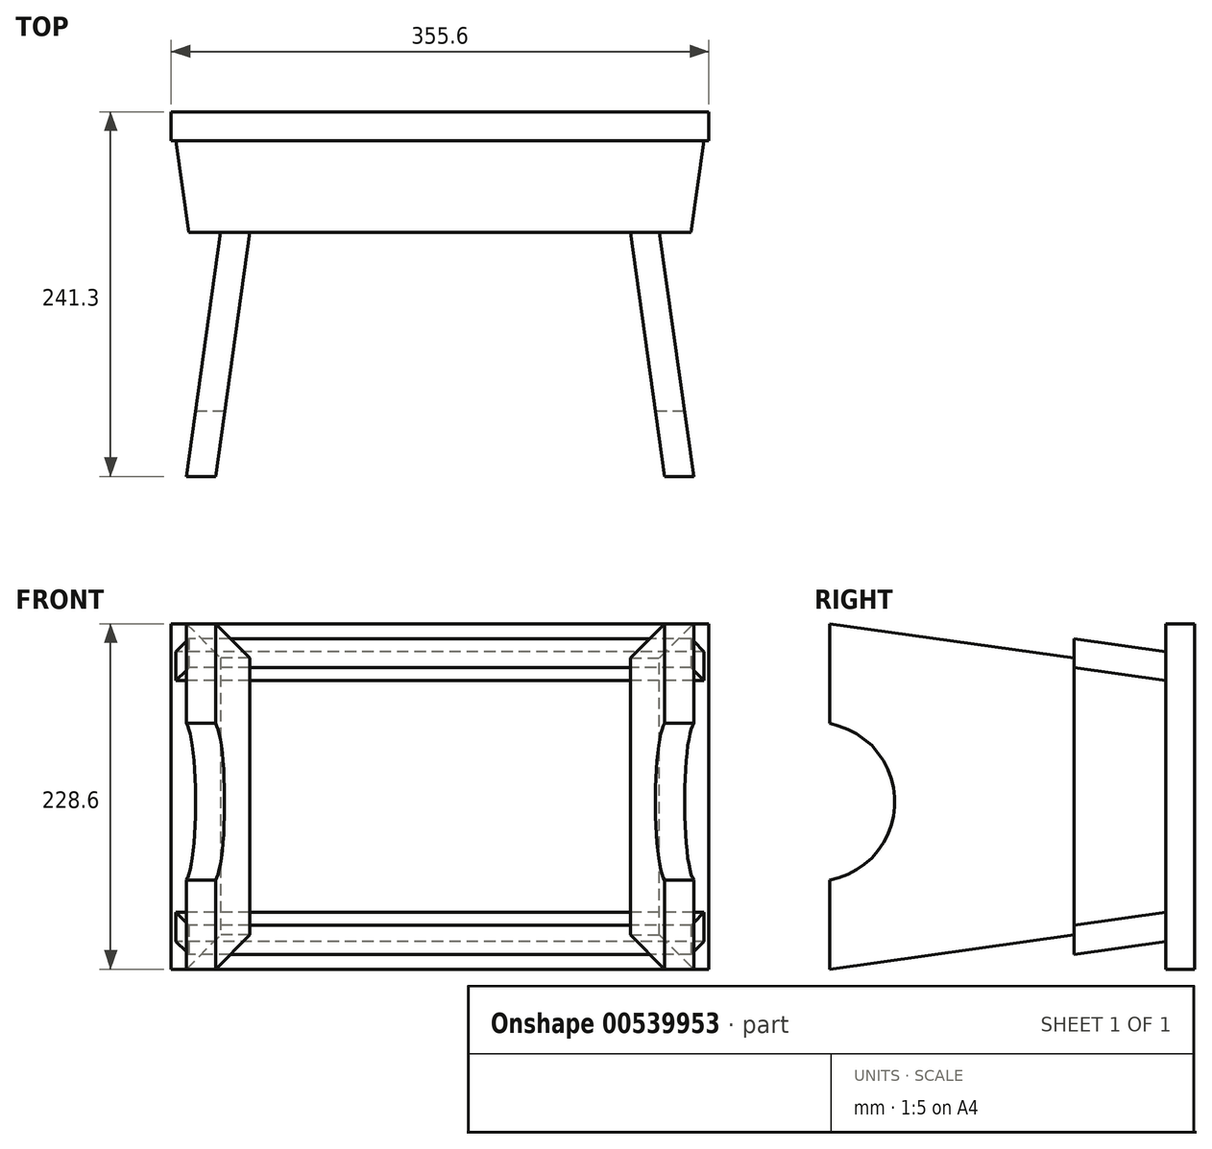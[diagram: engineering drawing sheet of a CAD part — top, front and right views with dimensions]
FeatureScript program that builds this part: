
annotation { "Feature Type Name" : "Feature", "Feature Type Description" : "" }
export const myFeature = defineFeature(function(context is Context, id is Id, definition is map)
    precondition{}
    {
        {
            var Q0;
            Q0=qCreatedBy(makeId("Top.planeOp"),FACE);
            var sketch = newSketch(context, id + "F0", { "sketchPlane" : qUnion([Q0])});
            skLineSegment(sketch, "E0.bottom", {"start": v(-177.8, -19.05) * mm, "end": v(177.8, -19.05) * mm});
            skLineSegment(sketch, "E0.top", {"start": v(-177.8, 0) * mm, "end": v(177.8, 0) * mm});
            skLineSegment(sketch, "E0.left", {"start": v(-177.8, 0) * mm, "end": v(-177.8, -19.05) * mm});
            skLineSegment(sketch, "E0.right", {"start": v(177.8, 0) * mm, "end": v(177.8, -19.05) * mm});
            skLineSegment(sketch, "E1.bottom", {"start": v(-177.8, 0) * mm, "end": v(-179.82, 0) * mm, "construction": true});
            skLineSegment(sketch, "E1.top", {"start": v(-177.8, 0) * mm, "end": v(-179.82, 0) * mm, "construction": true});
            skLineSegment(sketch, "E1.left", {"start": v(-179.82, 0) * mm, "end": v(-179.82, 0) * mm});
            skLineSegment(sketch, "E1.right", {"start": v(-177.8, 0) * mm, "end": v(-177.8, 0) * mm});
            skLineSegment(sketch, "E2.bottom", {"start": v(-177.8, 0) * mm, "end": v(177.8, 0) * mm, "construction": true});
            skLineSegment(sketch, "E2.top", {"start": v(-177.8, -241.3) * mm, "end": v(177.8, -241.3) * mm, "construction": true});
            skLineSegment(sketch, "E2.left", {"start": v(-177.8, 0) * mm, "end": v(-177.8, -241.3) * mm, "construction": true});
            skLineSegment(sketch, "E2.right", {"start": v(177.8, 0) * mm, "end": v(177.8, -241.3) * mm, "construction": true});
            skLineSegment(sketch, "E3", {"start": v(136.51, -19.05) * mm, "end": v(167.75, -241.3) * mm});
            skLineSegment(sketch, "E4", {"start": v(148.51, -241.3) * mm, "end": v(117.28, -19.05) * mm});
            skLineSegment(sketch, "E5", {"start": v(167.75, -241.3) * mm, "end": v(148.51, -241.3) * mm});
            skLineSegment(sketch, "E6", {"start": v(117.28, -19.05) * mm, "end": v(136.51, -19.05) * mm});
            skLineSegment(sketch, "E7", {"start": v(0, 0) * mm, "end": v(0, -241.3) * mm});
            skLineSegment(sketch, "E8", {"start": v(0, -241.3) * mm, "end": v(0, -244.61) * mm});
            skPoint(sketch, "E8.endSnap0", {"position": v(0, -120.65) * mm});
            skLineSegment(sketch, "E9.MirrorCS", {"start": v(-117.28, -19.05) * mm, "end": v(-136.51, -19.05) * mm});
            skLineSegment(sketch, "E10.MirrorCS", {"start": v(-167.75, -241.3) * mm, "end": v(-148.51, -241.3) * mm});
            skLineSegment(sketch, "E11.MirrorCS", {"start": v(-148.51, -241.3) * mm, "end": v(-117.28, -19.05) * mm});
            skLineSegment(sketch, "E12.MirrorCS", {"start": v(-136.51, -19.05) * mm, "end": v(-167.75, -241.3) * mm});
            skLineSegment(sketch, "E13", {"start": v(174.62, -19.05) * mm, "end": v(166.07, -79.9) * mm});
            skLineSegment(sketch, "E14.MirrorCS", {"start": v(-174.62, -19.05) * mm, "end": v(-166.07, -79.9) * mm});
            skLineSegment(sketch, "E15", {"start": v(-177.8, -79.9) * mm, "end": v(177.8, -79.9) * mm});
            skLineSegment(sketch, "E16", {"start": v(177.8, -79.9) * mm, "end": v(177.8, -19.05) * mm});
            skLineSegment(sketch, "E17", {"start": v(-177.8, -79.9) * mm, "end": v(-177.8, -19.05) * mm});
            skSolve(sketch);
        }
        {
            var Q0;
            Q0=makeQuery(id+"F0.imprint","IMPRINT",FACE,{"disambiguationData":[TD([[makeQuery(id+"F0.imprint","IMPRINT",EDGE,{"derivedFrom":sQuery(id+"F0.wireOp",EDGE,"E0.top")}),-1.0]])]});
            extrude(context, id + "F1", {"entities" : qUnion([Q0]), "depth" : 228.6 * mm, "offsetDistance" : 25.4 * mm, "symmetric" : true});
        }
        {
            var Q0;
            {var subQ0=sQuery(id+"F0.wireOp",EDGE,"E6");Q0=makeQuery(id+"F0.imprint","IMPRINT",FACE,{"disambiguationData":[TD([[makeQuery(id+"F0.imprint","IMPRINT",EDGE,{"derivedFrom":subQ0}),-1.0]])]});}
            var Q1;
            {var subQ0=sQuery(id+"F0.wireOp",EDGE,"E5");Q1=makeQuery(id+"F0.imprint","IMPRINT",FACE,{"disambiguationData":[TD([[makeQuery(id+"F0.imprint","IMPRINT",EDGE,{"derivedFrom":subQ0}),-1.0]])]});}
            var Q2;
            Q2=makeQuery(id+"F1.opExtrude","CAP_VERTEX",VERTEX,{"disambiguationData":[OSD([sQuery(id+"F0.wireOp",EDGE,"E0.top"),sQuery(id+"F0.wireOp",EDGE,"E0.right")])],"isStart":true});
            var Q3;
            Q3=makeQuery(id+"F1.opExtrude","CAP_VERTEX",VERTEX,{"disambiguationData":[OSD([sQuery(id+"F0.wireOp",EDGE,"E0.top"),sQuery(id+"F0.wireOp",EDGE,"E0.right")])],"isStart":false});
            extrude(context, id + "F2", {"entities" : qUnion([Q0, Q1]), "endBound" : BoundingType.UP_TO_VERTEX, "oppositeDirection" : true, "depth" : 25.4 * mm, "endBoundEntityVertex" : qUnion([Q2]), "offsetDistance" : 25.4 * mm, "hasSecondDirection" : true, "secondDirectionBound" : BoundingType.UP_TO_VERTEX, "secondDirectionOppositeDirection" : false, "secondDirectionDepth" : 25.4 * mm, "secondDirectionBoundEntityVertex" : qUnion([Q3])});
        }
        {
            var Q0;
            {var subQ0=sQuery(id+"F0.wireOp",EDGE,"E9.MirrorCS");Q0=makeQuery(id+"F0.imprint","IMPRINT",FACE,{"disambiguationData":[TD([[makeQuery(id+"F0.imprint","IMPRINT",EDGE,{"derivedFrom":subQ0}),1.0]])]});}
            var Q1;
            {var subQ0=sQuery(id+"F0.wireOp",EDGE,"E10.MirrorCS");Q1=makeQuery(id+"F0.imprint","IMPRINT",FACE,{"disambiguationData":[TD([[makeQuery(id+"F0.imprint","IMPRINT",EDGE,{"derivedFrom":subQ0}),1.0]])]});}
            var Q2;
            Q2=makeQuery(id+"F1.opExtrude","CAP_VERTEX",VERTEX,{"disambiguationData":[OSD([sQuery(id+"F0.wireOp",EDGE,"E0.top"),sQuery(id+"F0.wireOp",EDGE,"E0.left")])],"isStart":false});
            var Q3;
            Q3=makeQuery(id+"F1.opExtrude","CAP_VERTEX",VERTEX,{"disambiguationData":[OSD([sQuery(id+"F0.wireOp",EDGE,"E0.top"),sQuery(id+"F0.wireOp",EDGE,"E0.left")])],"isStart":true});
            extrude(context, id + "F3", {"entities" : qUnion([Q0, Q1]), "endBound" : BoundingType.UP_TO_VERTEX, "depth" : 25.4 * mm, "endBoundEntityVertex" : qUnion([Q2]), "offsetDistance" : 25.4 * mm, "hasSecondDirection" : true, "secondDirectionBound" : BoundingType.UP_TO_VERTEX, "secondDirectionOppositeDirection" : true, "secondDirectionDepth" : 25.4 * mm, "secondDirectionBoundEntityVertex" : qUnion([Q3])});
        }
        {
            var Q0;
            Q0=qCreatedBy(makeId("Right.planeOp"),FACE);
            var sketch = newSketch(context, id + "F4", { "sketchPlane" : qUnion([Q0])});
            skLineSegment(sketch, "E18.0.0", {"start": v(-19.05, -114.3) * mm, "end": v(-19.05, 114.3) * mm});
            skLineSegment(sketch, "E18.0.1", {"start": v(-19.05, 114.3) * mm, "end": v(-241.3, 114.3) * mm});
            skLineSegment(sketch, "E18.0.2", {"start": v(-241.3, 114.3) * mm, "end": v(-241.3, -114.3) * mm});
            skLineSegment(sketch, "E18.0.3", {"start": v(-241.3, -114.3) * mm, "end": v(-19.05, -114.3) * mm});
            skLineSegment(sketch, "E19", {"start": v(-241.3, 114.3) * mm, "end": v(-19.05, 83.06) * mm});
            skLineSegment(sketch, "E20.MirrorCS", {"start": v(-241.3, -114.3) * mm, "end": v(-19.05, -83.06) * mm});
            skArc(sketch, "E21", {"start": v(-241.3, -55.42) * mm, "mid": v(-198.1, -3.53) * mm, "end": v(-241.3, 48.35) * mm});
            skLineSegment(sketch, "E22", {"start": v(-250.87, -3.53) * mm, "end": v(-241.3, 0) * mm, "construction": true});
            skSolve(sketch);
        }
        {
            var Q0;
            {var subQ0=sQuery(id+"F4.wireOp",EDGE,"E21");Q0=makeQuery(id+"F4.imprint","IMPRINT",FACE,{"disambiguationData":[TD([[makeQuery(id+"F4.imprint","IMPRINT",EDGE,{"derivedFrom":subQ0}),1.0]])]});}
            var Q1;
            {var subQ0=sQuery(id+"F4.wireOp",EDGE,"E18.0.3");Q1=makeQuery(id+"F4.imprint","IMPRINT",FACE,{"disambiguationData":[TD([[makeQuery(id+"F4.imprint","IMPRINT",EDGE,{"derivedFrom":subQ0}),1.0]])]});}
            var Q2;
            {var subQ0=sQuery(id+"F4.wireOp",EDGE,"E18.0.1");Q2=makeQuery(id+"F4.imprint","IMPRINT",FACE,{"disambiguationData":[TD([[makeQuery(id+"F4.imprint","IMPRINT",EDGE,{"derivedFrom":subQ0}),1.0]])]});}
            extrude(context, id + "F5", {"entities" : qUnion([Q0, Q1, Q2]), "operationType" : NewBodyOperationType.REMOVE, "endBound" : BoundingType.THROUGH_ALL, "oppositeDirection" : true, "depth" : 25.4 * mm, "offsetDistance" : 25.4 * mm, "hasSecondDirection" : true, "secondDirectionBound" : BoundingType.THROUGH_ALL, "secondDirectionOppositeDirection" : false, "secondDirectionDepth" : 25.4 * mm});
        }
        {
            var Q0;
            Q0=qCreatedBy(makeId("Right.planeOp"),FACE);
            var sketch = newSketch(context, id + "F6", { "sketchPlane" : qUnion([Q0])});
            skLineSegment(sketch, "E23.0", {"start": v(-19.05, 83.06) * mm, "end": v(-241.3, 114.3) * mm});
            skLineSegment(sketch, "E24.0", {"start": v(-19.05, 114.3) * mm, "end": v(-19.05, -114.3) * mm});
            skLineSegment(sketch, "E25.0", {"start": v(-19.05, -83.06) * mm, "end": v(-241.3, -114.3) * mm});
            skLineSegment(sketch, "E26", {"start": v(-19.05, 95.89) * mm, "end": v(-79.9, 104.44) * mm});
            skLineSegment(sketch, "E27", {"start": v(-79.9, 104.44) * mm, "end": v(-79.9, 85.2) * mm});
            skLineSegment(sketch, "E28", {"start": v(-79.9, 85.2) * mm, "end": v(-19.05, 76.65) * mm});
            skLineSegment(sketch, "E29", {"start": v(-79.9, 85.2) * mm, "end": v(-79.9, -22.26) * mm, "construction": true});
            skLineSegment(sketch, "E30.MirrorCS", {"start": v(-79.9, -85.2) * mm, "end": v(-79.9, 22.26) * mm, "construction": true});
            skLineSegment(sketch, "E31.MirrorCS", {"start": v(-79.9, -85.2) * mm, "end": v(-19.05, -76.65) * mm});
            skLineSegment(sketch, "E32.MirrorCS", {"start": v(-19.05, -95.89) * mm, "end": v(-79.9, -104.44) * mm});
            skLineSegment(sketch, "E33.MirrorCS", {"start": v(-79.9, -104.44) * mm, "end": v(-79.9, -85.2) * mm});
            skSolve(sketch);
        }
        {
            var Q0;
            {var subQ3=sQuery(id+"F6.wireOp",EDGE,"E31.MirrorCS");Q0=makeQuery(id+"F6.imprint","IMPRINT",FACE,{"disambiguationData":[TD([[makeQuery(id+"F6.imprint","IMPRINT",EDGE,{"derivedFrom":subQ3}),-1.0]])]});}
            var Q1;
            {var subQ3=sQuery(id+"F6.wireOp",EDGE,"E32.MirrorCS");Q1=makeQuery(id+"F6.imprint","IMPRINT",FACE,{"disambiguationData":[TD([[makeQuery(id+"F6.imprint","IMPRINT",EDGE,{"derivedFrom":subQ3}),-1.0]])]});}
            var Q2;
            {var subQ5=sQuery(id+"F6.wireOp",EDGE,"E28");Q2=makeQuery(id+"F6.imprint","IMPRINT",FACE,{"disambiguationData":[TD([[makeQuery(id+"F6.imprint","IMPRINT",EDGE,{"derivedFrom":subQ5}),1.0]])]});}
            var Q3;
            {var subQ5=sQuery(id+"F6.wireOp",EDGE,"E26");Q3=makeQuery(id+"F6.imprint","IMPRINT",FACE,{"disambiguationData":[TD([[makeQuery(id+"F6.imprint","IMPRINT",EDGE,{"derivedFrom":subQ5}),1.0]])]});}
            var Q4;
            Q4=makeQuery(id+"F1.opExtrude","SWEPT_FACE",FACE,{"disambiguationData":[OSD([sQuery(id+"F0.wireOp",EDGE,"E0.left")])]});
            var Q5;
            Q5=makeQuery(id+"F1.opExtrude","CAP_VERTEX",VERTEX,{"disambiguationData":[OSD([sQuery(id+"F0.wireOp",EDGE,"E0.bottom"),sQuery(id+"F0.wireOp",EDGE,"E0.right")])],"isStart":true});
            var Q6;
            Q6=makeQuery(id+"F1.opExtrude","CAP_VERTEX",VERTEX,{"disambiguationData":[OSD([sQuery(id+"F0.wireOp",EDGE,"E0.bottom"),sQuery(id+"F0.wireOp",EDGE,"E0.left")])],"isStart":true});
            extrude(context, id + "F7", {"entities" : qUnion([Q0, Q1, Q2, Q3]), "endBound" : BoundingType.UP_TO_VERTEX, "depth" : 159 * mm, "endBoundEntityFace" : qUnion([Q4]), "endBoundEntityVertex" : qUnion([Q5]), "offsetDistance" : 25.4 * mm, "hasSecondDirection" : true, "secondDirectionBound" : BoundingType.UP_TO_VERTEX, "secondDirectionOppositeDirection" : true, "secondDirectionDepth" : 25.4 * mm, "secondDirectionBoundEntityVertex" : qUnion([Q6])});
        }
        {
            var Q0;
            {var subQ2=sQuery(id+"F0.wireOp",EDGE,"E13");Q0=makeQuery(id+"F0.imprint","IMPRINT",FACE,{"disambiguationData":[TD([[makeQuery(id+"F0.imprint","IMPRINT",EDGE,{"derivedFrom":subQ2}),1.0]])]});}
            var Q1;
            {var subQ2=sQuery(id+"F0.wireOp",EDGE,"E14.MirrorCS");Q1=makeQuery(id+"F0.imprint","IMPRINT",FACE,{"disambiguationData":[TD([[makeQuery(id+"F0.imprint","IMPRINT",EDGE,{"derivedFrom":subQ2}),-1.0]])]});}
            var Q2;
            Q2=sQuery(id+"F0.wireOp",EDGE,"E13");
            var Q3;
            Q3=sQuery(id+"F0.wireOp",EDGE,"E16");
            var Q4;
            Q4=makeQuery(id+"F1.opExtrude","CAP_FACE",FACE,{"disambiguationData":[OSD([sQuery(id+"F0.wireOp",EDGE,"E0.bottom"),sQuery(id+"F0.wireOp",EDGE,"E0.top"),sQuery(id+"F0.wireOp",EDGE,"E0.left"),sQuery(id+"F0.wireOp",EDGE,"E0.right"),sQuery(id+"F0.wireOp",EDGE,"E6"),sQuery(id+"F0.wireOp",EDGE,"E9.MirrorCS")])],"isStart":false});
            var Q5;
            Q5=makeQuery(id+"F1.opExtrude","CAP_FACE",FACE,{"disambiguationData":[OSD([sQuery(id+"F0.wireOp",EDGE,"E0.bottom"),sQuery(id+"F0.wireOp",EDGE,"E0.top"),sQuery(id+"F0.wireOp",EDGE,"E0.left"),sQuery(id+"F0.wireOp",EDGE,"E0.right"),sQuery(id+"F0.wireOp",EDGE,"E6"),sQuery(id+"F0.wireOp",EDGE,"E9.MirrorCS")])],"isStart":true});
            extrude(context, id + "F8", {"entities" : qUnion([Q0, Q1]), "operationType" : NewBodyOperationType.REMOVE, "surfaceEntities" : qUnion([Q2, Q3]), "endBound" : BoundingType.UP_TO_SURFACE, "depth" : 25.4 * mm, "endBoundEntityFace" : qUnion([Q4]), "offsetDistance" : 25.4 * mm, "hasSecondDirection" : true, "secondDirectionBound" : BoundingType.UP_TO_SURFACE, "secondDirectionOppositeDirection" : true, "secondDirectionDepth" : 25.4 * mm, "secondDirectionBoundEntityFace" : qUnion([Q5])});
        }
        {
            var Q0;
            Q0=makeQuery(id+"F3.opExtrude","SWEPT_BODY",BODY,{"disambiguationData":[OSD([sQuery(id+"F0.wireOp",EDGE,"E9.MirrorCS"),sQuery(id+"F0.wireOp",EDGE,"E10.MirrorCS"),sQuery(id+"F0.wireOp",EDGE,"E11.MirrorCS"),sQuery(id+"F0.wireOp",EDGE,"E12.MirrorCS")])]});
            var Q1;
            Q1=makeQuery(id+"F7.opExtrude","SWEPT_BODY",BODY,{"disambiguationData":[OSD([sQuery(id+"F6.wireOp",EDGE,"E24.0"),sQuery(id+"F6.wireOp",EDGE,"E26"),sQuery(id+"F6.wireOp",EDGE,"E27"),sQuery(id+"F6.wireOp",EDGE,"E28")])]});
            booleanBodies(context, id + "F9", {"operationType" : BooleanOperationType.SUBTRACTION, "tools" : qUnion([Q0]), "targets" : qUnion([Q1]), "keepTools" : true});
        }
        {
            var Q0;
            Q0=makeQuery(id+"F2.opExtrude","SWEPT_BODY",BODY,{"disambiguationData":[OSD([sQuery(id+"F0.wireOp",EDGE,"E3"),sQuery(id+"F0.wireOp",EDGE,"E4"),sQuery(id+"F0.wireOp",EDGE,"E5"),sQuery(id+"F0.wireOp",EDGE,"E6")])]});
            var Q1;
            Q1=makeQuery(id+"F7.opExtrude","SWEPT_BODY",BODY,{"disambiguationData":[OSD([sQuery(id+"F6.wireOp",EDGE,"E24.0"),sQuery(id+"F6.wireOp",EDGE,"E26"),sQuery(id+"F6.wireOp",EDGE,"E27"),sQuery(id+"F6.wireOp",EDGE,"E28")])]});
            booleanBodies(context, id + "F10", {"operationType" : BooleanOperationType.SUBTRACTION, "tools" : qUnion([Q0]), "targets" : qUnion([Q1]), "keepTools" : true});
        }
        {
            var Q0;
            Q0=makeQuery(id+"F2.opExtrude","SWEPT_BODY",BODY,{"disambiguationData":[OSD([sQuery(id+"F0.wireOp",EDGE,"E3"),sQuery(id+"F0.wireOp",EDGE,"E4"),sQuery(id+"F0.wireOp",EDGE,"E5"),sQuery(id+"F0.wireOp",EDGE,"E6")])]});
            var Q1;
            Q1=makeQuery(id+"F7.opExtrude","SWEPT_BODY",BODY,{"disambiguationData":[OSD([sQuery(id+"F6.wireOp",EDGE,"E24.0"),sQuery(id+"F6.wireOp",EDGE,"E31.MirrorCS"),sQuery(id+"F6.wireOp",EDGE,"E32.MirrorCS"),sQuery(id+"F6.wireOp",EDGE,"E33.MirrorCS")])]});
            booleanBodies(context, id + "F11", {"operationType" : BooleanOperationType.SUBTRACTION, "tools" : qUnion([Q0]), "targets" : qUnion([Q1]), "keepTools" : true});
        }
        {
            var Q0;
            Q0=makeQuery(id+"F3.opExtrude","SWEPT_BODY",BODY,{"disambiguationData":[OSD([sQuery(id+"F0.wireOp",EDGE,"E9.MirrorCS"),sQuery(id+"F0.wireOp",EDGE,"E10.MirrorCS"),sQuery(id+"F0.wireOp",EDGE,"E11.MirrorCS"),sQuery(id+"F0.wireOp",EDGE,"E12.MirrorCS")])]});
            var Q1;
            Q1=makeQuery(id+"F7.opExtrude","SWEPT_BODY",BODY,{"disambiguationData":[OSD([sQuery(id+"F6.wireOp",EDGE,"E24.0"),sQuery(id+"F6.wireOp",EDGE,"E31.MirrorCS"),sQuery(id+"F6.wireOp",EDGE,"E32.MirrorCS"),sQuery(id+"F6.wireOp",EDGE,"E33.MirrorCS")])]});
            booleanBodies(context, id + "F12", {"operationType" : BooleanOperationType.SUBTRACTION, "tools" : qUnion([Q0]), "targets" : qUnion([Q1]), "keepTools" : true});
        }
    });
